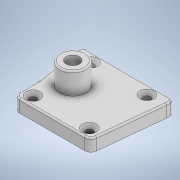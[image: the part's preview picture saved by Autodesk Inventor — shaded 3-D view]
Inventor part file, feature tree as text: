
AUTODESK INVENTOR PART (.ipt)
format: ipt  version: 2020.3 (Build 243373000, 373)  size: 234,496 bytes
history: native  units: mm
features: other x3, sketch x2
ambient origin geometry x8: Origin, YZ Plane, XZ Plane, XY Plane, X Axis, Y Axis, Z Axis, Center Point
bodies: Solid1 (feature_tree)
feature tree (5):
  other  "LegPin_Side_v1.ipt"
  other  "Solid6::LegPin_Side_v1.ipt"
  other  "TaggingFeature1"
  sketch  "Sketch1"  dims[d0=10.0mm]
  sketch  "Sketch2"
